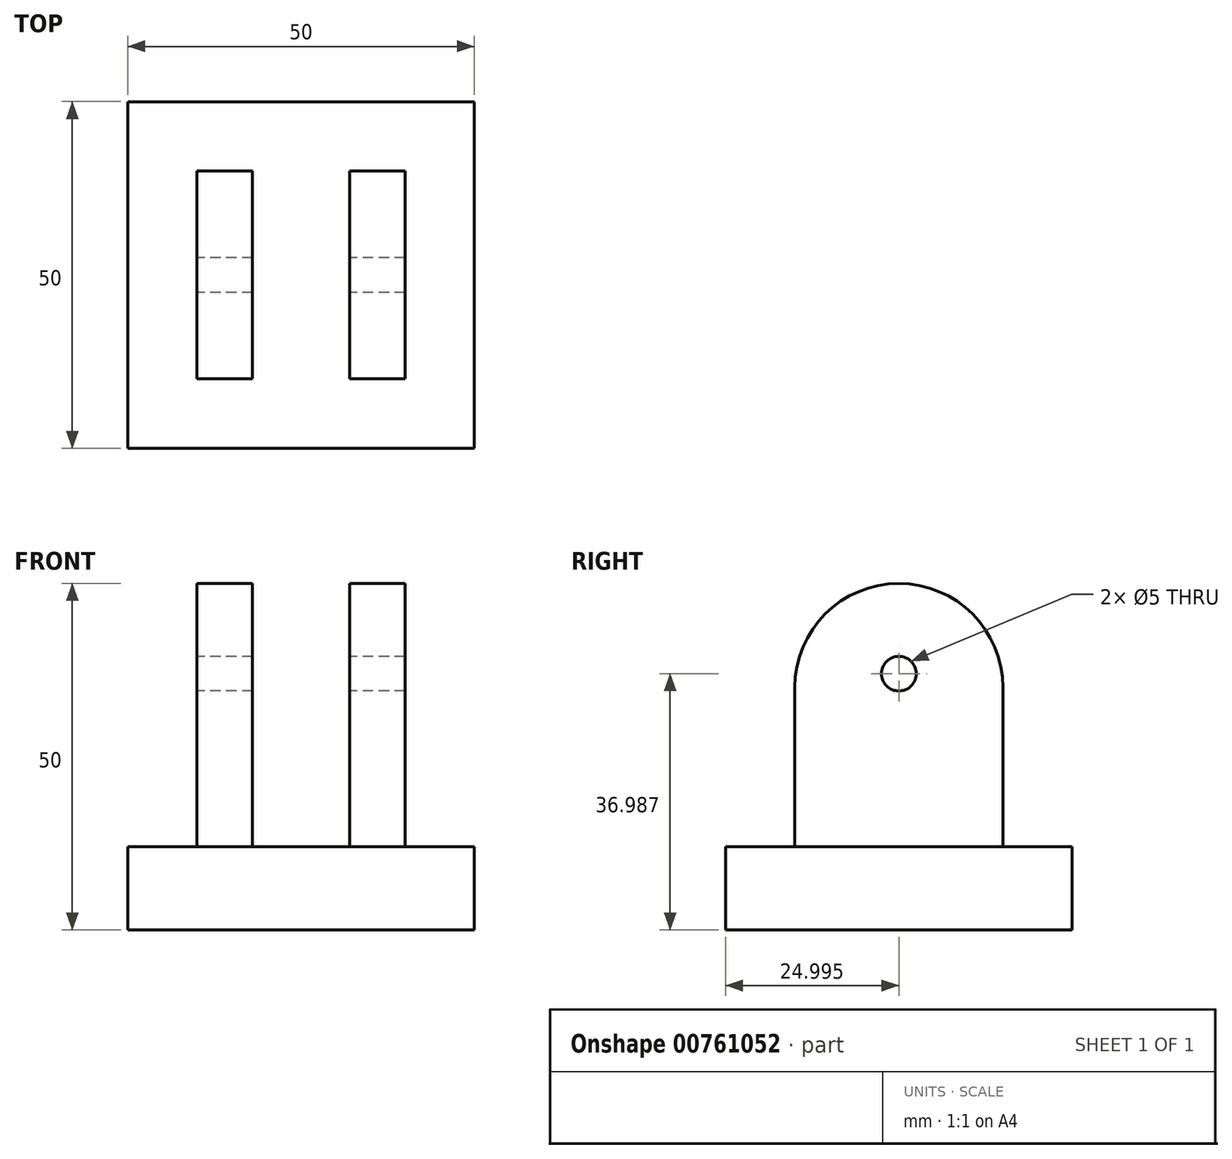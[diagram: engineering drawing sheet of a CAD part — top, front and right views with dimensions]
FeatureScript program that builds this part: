
annotation { "Feature Type Name" : "Feature", "Feature Type Description" : "" }
export const myFeature = defineFeature(function(context is Context, id is Id, definition is map)
    precondition{}
    {
        {
            var Q0;
            Q0=qCreatedBy(makeId("Top.planeOp"),FACE);
            var sketch = newSketch(context, id + "F0", { "sketchPlane" : qUnion([Q0])});
            skLineSegment(sketch, "E0.bottom", {"start": v(-28.1, 26.33) * mm, "end": v(21.9, 26.33) * mm});
            skLineSegment(sketch, "E0.top", {"start": v(-28.1, -23.67) * mm, "end": v(21.9, -23.67) * mm});
            skLineSegment(sketch, "E0.left", {"start": v(-28.1, 26.33) * mm, "end": v(-28.1, -23.67) * mm});
            skLineSegment(sketch, "E0.right", {"start": v(21.9, 26.33) * mm, "end": v(21.9, -23.67) * mm});
            skSolve(sketch);
        }
        {
            var Q0;
            Q0=makeQuery(id+"F0.imprint","IMPRINT",FACE,{"disambiguationData":[TD([[makeQuery(id+"F0.imprint","IMPRINT",EDGE,{"derivedFrom":sQuery(id+"F0.wireOp",EDGE,"E0.bottom")}),-1.0]])]});
            extrude(context, id + "F1", {"entities" : qUnion([Q0]), "depth" : 10 * mm, "offsetDistance" : 25 * mm});
        }
        {
            var Q0;
            Q0=makeQuery(id+"F1.opExtrude","CAP_FACE",FACE,{"disambiguationData":[OSD([sQuery(id+"F0.wireOp",EDGE,"E0.bottom"),sQuery(id+"F0.wireOp",EDGE,"E0.top"),sQuery(id+"F0.wireOp",EDGE,"E0.left"),sQuery(id+"F0.wireOp",EDGE,"E0.right")])],"isStart":false});
            var sketch = newSketch(context, id + "F2", { "sketchPlane" : qUnion([Q0])});
            skLineSegment(sketch, "E1.bottom", {"start": v(-18.1, 16.33) * mm, "end": v(-10.1, 16.33) * mm});
            skLineSegment(sketch, "E1.top", {"start": v(-18.1, -13.67) * mm, "end": v(-10.1, -13.67) * mm});
            skLineSegment(sketch, "E1.left", {"start": v(-18.1, 16.33) * mm, "end": v(-18.1, -13.67) * mm});
            skLineSegment(sketch, "E1.right", {"start": v(-10.1, 16.33) * mm, "end": v(-10.1, -13.67) * mm});
            skSolve(sketch);
        }
        {
            var Q0;
            Q0=makeQuery(id+"F2.imprint","IMPRINT",FACE,{"disambiguationData":[TD([[makeQuery(id+"F2.imprint","IMPRINT",EDGE,{"derivedFrom":sQuery(id+"F2.wireOp",EDGE,"E1.bottom")}),1.0]])]});
            var sketch = newSketch(context, id + "F3", { "sketchPlane" : qUnion([Q0])});
            skLineSegment(sketch, "E2.bottom", {"start": v(3.9, 16.33) * mm, "end": v(11.9, 16.33) * mm});
            skLineSegment(sketch, "E2.top", {"start": v(3.9, -13.67) * mm, "end": v(11.9, -13.67) * mm});
            skLineSegment(sketch, "E2.left", {"start": v(3.9, 16.33) * mm, "end": v(3.9, -13.67) * mm});
            skLineSegment(sketch, "E2.right", {"start": v(11.9, 16.33) * mm, "end": v(11.9, -13.67) * mm});
            skSolve(sketch);
        }
        {
            var Q0;
            Q0=makeQuery(id+"F2.imprint","IMPRINT",FACE,{"disambiguationData":[TD([[makeQuery(id+"F2.imprint","IMPRINT",EDGE,{"derivedFrom":sQuery(id+"F2.wireOp",EDGE,"E1.bottom")}),-1.0]])]});
            extrude(context, id + "F4", {"entities" : qUnion([Q0]), "operationType" : NewBodyOperationType.ADD, "depth" : 40 * mm, "offsetDistance" : 25 * mm});
        }
        {
            var Q0;
            Q0=makeQuery(id+"F3.imprint","IMPRINT",FACE,{"disambiguationData":[TD([[makeQuery(id+"F3.imprint","IMPRINT",EDGE,{"derivedFrom":sQuery(id+"F3.wireOp",EDGE,"E2.bottom")}),-1.0]])]});
            extrude(context, id + "F5", {"entities" : qUnion([Q0]), "operationType" : NewBodyOperationType.ADD, "depth" : 40 * mm, "offsetDistance" : 25 * mm});
        }
        {
            var Q0;
            Q0=makeQuery(id+"F5.opExtrude","CAP_EDGE",EDGE,{"disambiguationData":[OSD([sQuery(id+"F3.wireOp",EDGE,"E2.top")])],"isStart":false});
            var Q1;
            Q1=makeQuery(id+"F5.opExtrude","CAP_EDGE",EDGE,{"disambiguationData":[OSD([sQuery(id+"F3.wireOp",EDGE,"E2.bottom")])],"isStart":false});
            var Q2;
            Q2=makeQuery(id+"F4.opExtrude","CAP_EDGE",EDGE,{"disambiguationData":[OSD([sQuery(id+"F2.wireOp",EDGE,"E1.top")])],"isStart":false});
            var Q3;
            Q3=makeQuery(id+"F4.opExtrude","CAP_EDGE",EDGE,{"disambiguationData":[OSD([sQuery(id+"F2.wireOp",EDGE,"E1.bottom")])],"isStart":false});
            fillet(context, id + "F6", {"entities" : qUnion([Q0, Q1, Q2, Q3]), "radius" : 15 * mm, "tangentPropagation" : true, "allowEdgeOverflow" : false});
        }
        {
            var Q0;
            Q0=makeQuery(id+"F4.opExtrude","SWEPT_FACE",FACE,{"disambiguationData":[OSD([sQuery(id+"F2.wireOp",EDGE,"E1.left")])]});
            var sketch = newSketch(context, id + "F7", { "sketchPlane" : qUnion([Q0])});
            skCircle(sketch, "E3", {"center": v(-1.33, 36.99) * mm, "radius": 2.5 * mm});
            skPoint(sketch, "E3.centerSnap0", {"position": v(-1.33, 50) * mm});
            skSolve(sketch);
        }
        {
            var Q0;
            Q0=sQuery(id+"F7.wireOp",VERTEX,"E3.center");
            var Q1;
            Q1=makeQuery(id+"F1.opExtrude","SWEPT_BODY",BODY,{"disambiguationData":[OSD([sQuery(id+"F0.wireOp",EDGE,"E0.bottom"),sQuery(id+"F0.wireOp",EDGE,"E0.top"),sQuery(id+"F0.wireOp",EDGE,"E0.left"),sQuery(id+"F0.wireOp",EDGE,"E0.right")])]});
            hole(context, id + "F8", {"style" : HoleStyle.SIMPLE, "endStyle" : HoleEndStyle.THROUGH, "holeDiameter" : 5 * mm, "majorDiameter" : 5 * mm, "isTappedThrough" : true, "tappedDepth" : 12 * mm, "tapClearance" : 3, "locations" : qUnion([Q0]), "scope" : qUnion([Q1])});
        }
        {
            var Q0;
            Q0=makeQuery(id+"F1.opExtrude","CAP_FACE",FACE,{"disambiguationData":[OSD([sQuery(id+"F0.wireOp",EDGE,"E0.bottom"),sQuery(id+"F0.wireOp",EDGE,"E0.top"),sQuery(id+"F0.wireOp",EDGE,"E0.left"),sQuery(id+"F0.wireOp",EDGE,"E0.right")])],"isStart":false});
            extrude(context, id + "F9", {"entities" : qUnion([Q0]), "operationType" : NewBodyOperationType.ADD, "depth" : 2 * mm, "offsetDistance" : 25 * mm});
        }
    });
